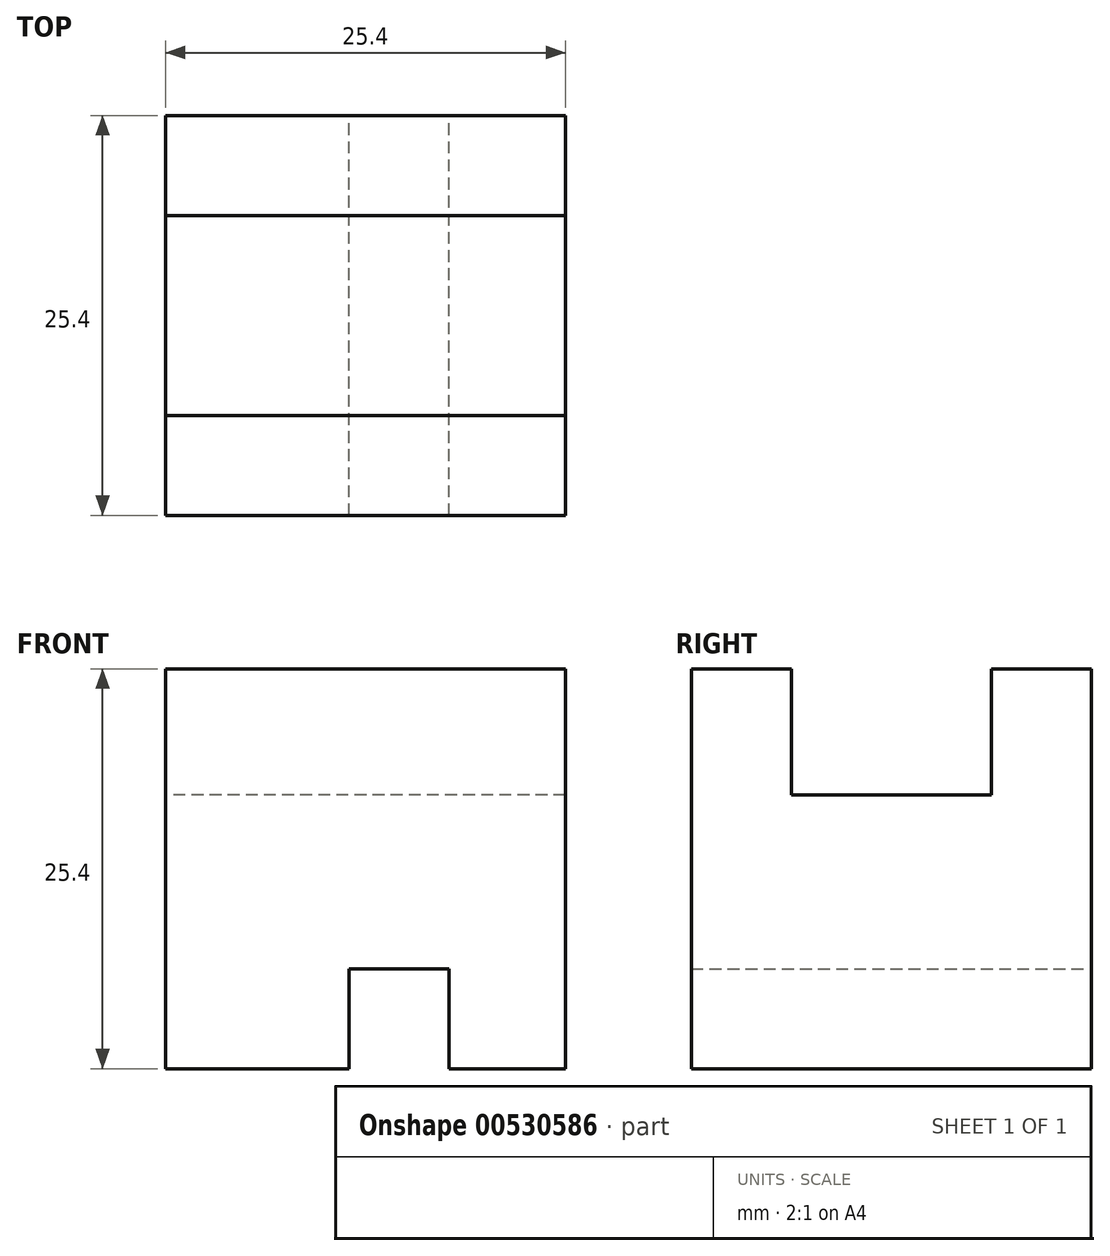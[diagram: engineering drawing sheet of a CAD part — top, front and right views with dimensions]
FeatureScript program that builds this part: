
annotation { "Feature Type Name" : "Feature", "Feature Type Description" : "" }
export const myFeature = defineFeature(function(context is Context, id is Id, definition is map)
    precondition{}
    {
        {
            var Q0;
            Q0=qCreatedBy(makeId("Right.planeOp"),FACE);
            var sketch = newSketch(context, id + "F0", { "sketchPlane" : qUnion([Q0])});
            skLineSegment(sketch, "E0", {"start": v(-22.33, 34.32) * mm, "end": v(-15.98, 34.32) * mm});
            skLineSegment(sketch, "E1", {"start": v(-15.98, 34.32) * mm, "end": v(-15.98, 26.3) * mm});
            skLineSegment(sketch, "E2", {"start": v(-15.98, 26.3) * mm, "end": v(-3.28, 26.3) * mm});
            skLineSegment(sketch, "E3", {"start": v(-3.28, 26.3) * mm, "end": v(-3.28, 34.32) * mm});
            skLineSegment(sketch, "E4", {"start": v(-3.28, 34.32) * mm, "end": v(3.07, 34.32) * mm});
            skLineSegment(sketch, "E5", {"start": v(3.07, 34.32) * mm, "end": v(3.07, 8.92) * mm});
            skLineSegment(sketch, "E6", {"start": v(-22.33, 34.32) * mm, "end": v(-22.33, 8.92) * mm});
            skLineSegment(sketch, "E7", {"start": v(-22.33, 8.92) * mm, "end": v(3.07, 8.92) * mm});
            skSolve(sketch);
        }
        {
            var Q0;
            Q0 = qSketchRegion(id + "F0", true);
            extrude(context, id + "F1", {"entities" : qUnion([Q0]), "depth" : 25.4 * mm, "offsetDistance" : 25.4 * mm});
        }
        {
            var Q0;
            Q0=makeQuery(id+"F1.opExtrude","SWEPT_FACE",FACE,{"disambiguationData":[OSD([sQuery(id+"F0.wireOp",EDGE,"E5")])]});
            var sketch = newSketch(context, id + "F2", { "sketchPlane" : qUnion([Q0])});
            skLineSegment(sketch, "E8", {"start": v(-18.01, 8.92) * mm, "end": v(-18.01, 15.27) * mm});
            skLineSegment(sketch, "E9", {"start": v(-18.01, 15.27) * mm, "end": v(-11.66, 15.27) * mm});
            skLineSegment(sketch, "E10", {"start": v(-11.66, 15.27) * mm, "end": v(-11.66, 8.92) * mm});
            skSolve(sketch);
        }
        {
            var Q0;
            {var subQ0=sQuery(id+"F2.wireOp",EDGE,"E8");Q0=makeQuery(id+"F2.imprint","IMPRINT",FACE,{"disambiguationData":[TD([[makeQuery(id+"F2.imprint","IMPRINT",EDGE,{"derivedFrom":subQ0}),-1.0]])]});}
            extrude(context, id + "F3", {"entities" : qUnion([Q0]), "operationType" : NewBodyOperationType.REMOVE, "oppositeDirection" : true, "depth" : 25.4 * mm, "offsetDistance" : 25.4 * mm});
        }
    });
